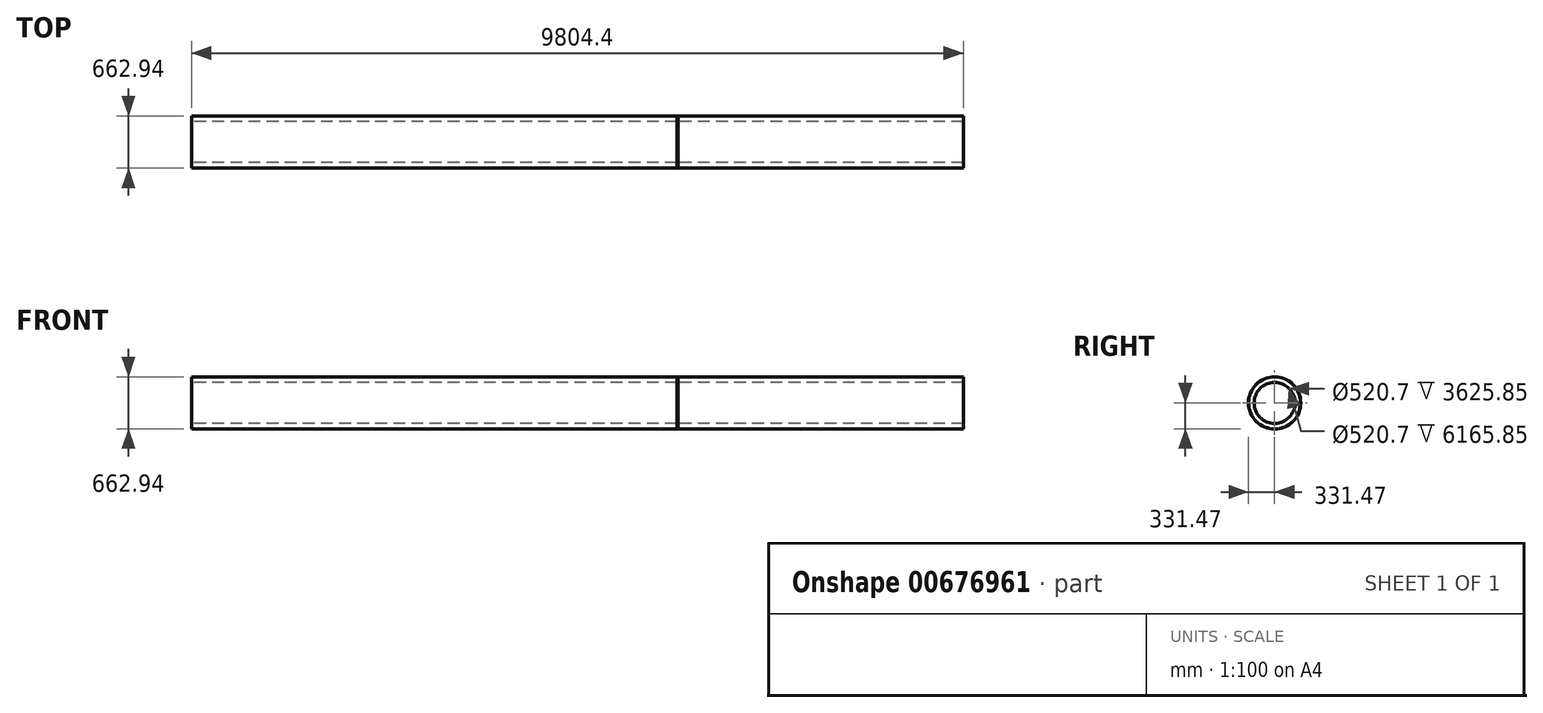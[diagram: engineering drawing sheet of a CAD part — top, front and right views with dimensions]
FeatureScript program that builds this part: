
annotation { "Feature Type Name" : "Feature", "Feature Type Description" : "" }
export const myFeature = defineFeature(function(context is Context, id is Id, definition is map)
    precondition{}
    {
        {
            var Q0;
            Q0=qCreatedBy(makeId("Right.planeOp"),FACE);
            var sketch = newSketch(context, id + "F0", { "sketchPlane" : qUnion([Q0])});
            skCircle(sketch, "E0", {"center": v(0, 0) * mm, "radius": 330.2 * mm});
            skSolve(sketch);
        }
        {
            var Q0;
            Q0=makeQuery(id+"F0.imprint","IMPRINT",FACE,{"disambiguationData":[TD([[makeQuery(id+"F0.imprint","IMPRINT",EDGE,{"derivedFrom":sQuery(id+"F0.wireOp",EDGE,"E0")}),1.0]])]});
            extrude(context, id + "F1", {"entities" : qUnion([Q0]), "endBound" : BoundingType.SYMMETRIC, "depth" : 9804.4 * mm, "offsetDistance" : 25.4 * mm});
        }
        {
            var Q0;
            Q0=qCreatedBy(makeId("Right.planeOp"),FACE);
            var sketch = newSketch(context, id + "F2", { "sketchPlane" : qUnion([Q0])});
            skCircle(sketch, "E1", {"center": v(0, 0) * mm, "radius": 260.35 * mm});
            skSolve(sketch);
        }
        {
            var Q0;
            Q0 = qSketchRegion(id + "F2", true);
            extrude(context, id + "F3", {"entities" : qUnion([Q0]), "operationType" : NewBodyOperationType.REMOVE, "endBound" : BoundingType.SYMMETRIC, "depth" : 10160 * mm, "offsetDistance" : 25.4 * mm});
        }
        {
            var Q0;
            Q0=qCreatedBy(makeId("Right.planeOp"),FACE);
            cPlane(context, id + "F4", {"entities" : qUnion([Q0]), "cplaneType" : CPlaneType.OFFSET, "offset" : 1270 * mm, "width" : 152.4 * mm, "height" : 152.4 * mm});
        }
        {
            var Q0;
            Q0=qCreatedBy(id+"F4.planeOp",FACE);
            var sketch = newSketch(context, id + "F5", { "sketchPlane" : qUnion([Q0])});
            skCircle(sketch, "E2", {"center": v(0, 0) * mm, "radius": 331.47 * mm});
            skSolve(sketch);
        }
        {
            var Q0;
            Q0 = qSketchRegion(id + "F5", true);
            extrude(context, id + "F6", {"entities" : qUnion([Q0]), "operationType" : NewBodyOperationType.ADD, "endBound" : BoundingType.SYMMETRIC, "depth" : 12.7 * mm, "offsetDistance" : 25.4 * mm});
        }
    });
